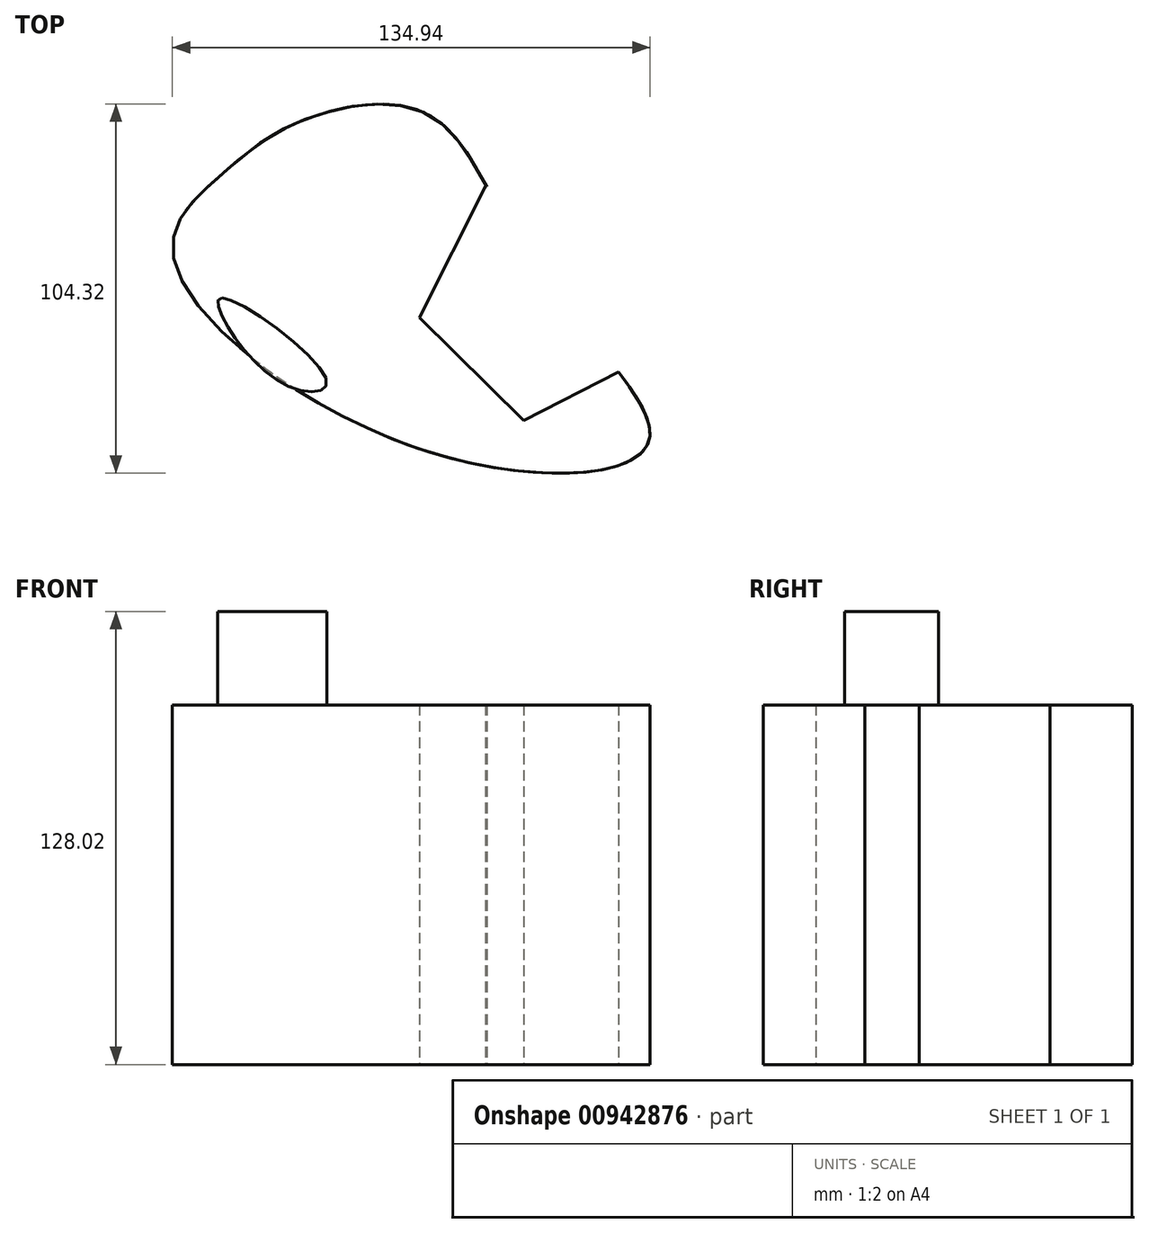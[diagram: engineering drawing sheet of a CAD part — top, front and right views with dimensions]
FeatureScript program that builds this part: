
annotation { "Feature Type Name" : "Feature", "Feature Type Description" : "" }
export const myFeature = defineFeature(function(context is Context, id is Id, definition is map)
    precondition{}
    {
        {
            var Q0;
            Q0=qCreatedBy(makeId("Top.planeOp"),FACE);
            var sketch = newSketch(context, id + "F0", { "sketchPlane" : qUnion([Q0])});
            skFitSpline(sketch, "E0", {"points": [v(-61.43, 8.67) * mm, v(11, -47.33) * mm, v(73.1, -44.16) * mm, v(40.48, 5.2) * mm, v(10.16, 48.33) * mm, v(-26.78, 45.54) * mm, v(-47.46, 31.25) * mm, v(-61.43, 8.67) * mm]});
            skFitSpline(sketch, "E1.0", {"points": [v(-54.93, 10.07) * mm, v(-54.88, 9.47) * mm, v(-54.78, 8.83) * mm, v(-54.57, 7.89) * mm, v(-54.17, 6.58) * mm, v(-53.41, 4.81) * mm, v(-52.05, 2.25) * mm, v(-49.67, -1.28) * mm, v(-45.82, -5.82) * mm, v(-41.07, -10.53) * mm, v(-35.53, -15.27) * mm, v(-29.3, -19.97) * mm, v(-20.25, -26.02) * mm, v(-10.25, -31.61) * mm, v(0.25, -36.41) * mm, v(6.93, -39.02) * mm, v(12.3, -40.83) * mm, v(17.67, -42.46) * mm, v(24.37, -44.13) * mm, v(32.22, -45.58) * mm, v(39.73, -46.47) * mm, v(46.72, -46.82) * mm, v(53.01, -46.64) * mm, v(58.42, -45.97) * mm, v(61.98, -45.07) * mm, v(64.13, -44.23) * mm, v(65.36, -43.59) * mm, v(66.19, -43) * mm, v(66.55, -42.64) * mm, v(66.7, -42.45) * mm, v(66.75, -42.36) * mm, v(66.76, -42.33) * mm, v(66.77, -42.31) * mm, v(66.77, -42.3) * mm, v(66.78, -42.26) * mm, v(66.8, -42.1) * mm, v(66.79, -41.64) * mm, v(66.58, -40.68) * mm, v(66.11, -39.36) * mm, v(65.36, -37.76) * mm, v(64, -35.32) * mm, v(61.64, -31.81) * mm, v(58.01, -27.09) * mm, v(53.8, -21.98) * mm, v(49.22, -16.56) * mm, v(45.27, -11.85) * mm, v(42.13, -7.98) * mm, v(39.8, -5.03) * mm, v(37.54, -2.05) * mm, v(35.71, 0.48) * mm, v(34.31, 2.51) * mm, v(32.96, 4.54) * mm, v(31.35, 7.06) * mm, v(29.54, 10.04) * mm, v(27.26, 13.95) * mm, v(24.65, 18.67) * mm, v(21.79, 23.98) * mm, v(19.1, 28.82) * mm, v(16.5, 33.1) * mm, v(13.93, 36.69) * mm, v(11.82, 39.05) * mm, v(10.12, 40.55) * mm, v(8.85, 41.5) * mm, v(7.77, 42.15) * mm, v(6.88, 42.6) * mm, v(5.94, 43) * mm, v(4.67, 43.44) * mm, v(2.45, 44) * mm, v(-0.66, 44.4) * mm, v(-4.78, 44.4) * mm, v(-9.11, 43.93) * mm, v(-13.51, 43.07) * mm, v(-17.1, 42.09) * mm, v(-19.84, 41.18) * mm, v(-21.82, 40.45) * mm, v(-23.7, 39.7) * mm, v(-25.44, 38.9) * mm, v(-27.08, 38.1) * mm, v(-29.14, 37) * mm, v(-31.53, 35.55) * mm, v(-34.22, 33.67) * mm, v(-36.86, 31.61) * mm, v(-39.11, 29.73) * mm, v(-41, 28.11) * mm, v(-42.46, 26.85) * mm, v(-43.99, 25.53) * mm, v(-45.5, 24.22) * mm, v(-46.97, 22.9) * mm, v(-48.85, 21.15) * mm, v(-50.97, 18.96) * mm, v(-52.64, 16.81) * mm, v(-53.64, 15.17) * mm, v(-54.21, 13.99) * mm, v(-54.62, 12.86) * mm, v(-54.86, 11.75) * mm, v(-54.94, 10.83) * mm, v(-54.93, 10.07) * mm, v(-54.88, 9.47) * mm, v(-54.78, 8.83) * mm, v(-54.93, 10.07) * mm]});
            skCircle(sketch, "E2.cCircle", {"center": v(43.03, -3.61) * mm, "radius": 28.54 * mm, "construction": true});
            skLineSegment(sketch, "E2.0", {"start": v(74.54, -19.48) * mm, "end": v(37.67, -38.48) * mm});
            skLineSegment(sketch, "E2.1", {"start": v(37.67, -38.48) * mm, "end": v(8.21, -9.3) * mm});
            skLineSegment(sketch, "E2.2", {"start": v(8.21, -9.3) * mm, "end": v(26.87, 27.75) * mm});
            skLineSegment(sketch, "E2.3", {"start": v(26.87, 27.75) * mm, "end": v(67.86, 21.45) * mm});
            skLineSegment(sketch, "E2.4", {"start": v(67.86, 21.45) * mm, "end": v(74.54, -19.48) * mm});
            skPoint(sketch, "E2.0.midPoint", {"position": v(56.1, -28.98) * mm});
            skSolve(sketch);
        }
        {
            var Q0;
            {var subQ5=sQuery(id+"F0.wireOp",EDGE,"E2.0");var subQ6=sQuery(id+"F0.wireOp",EDGE,"E0");var subQ7=makeQuery(id+"F0.imprint","INTERSECT",VERTEX,{"derivedFrom":[subQ6,subQ5]});Q0=makeQuery(id+"F0.imprint","IMPRINT",FACE,{"disambiguationData":[TD([[makeQuery(id+"F0.imprint","IMPRINT",EDGE,{"disambiguationData":[TD([[subQ7,1.0]])],"derivedFrom":subQ6}),1.0]])]});}
            extrude(context, id + "F1", {"entities" : qUnion([Q0]), "depth" : 25.4 * mm, "offsetDistance" : 25.4 * mm});
        }
        {
            var Q0;
            Q0=makeQuery(id+"F1.opExtrude","CAP_FACE",FACE,{"disambiguationData":[OSD([sQuery(id+"F0.wireOp",EDGE,"E0"),sQuery(id+"F0.wireOp",EDGE,"E1.0"),sQuery(id+"F0.wireOp",EDGE,"E2.0"),sQuery(id+"F0.wireOp",EDGE,"E2.2"),sQuery(id+"F0.wireOp",EDGE,"E2.3")])],"isStart":false});
            extrude(context, id + "F2", {"entities" : qUnion([Q0]), "operationType" : NewBodyOperationType.ADD, "depth" : 76.2 * mm, "offsetDistance" : 25.4 * mm});
        }
        {
            var Q0;
            Q0=makeQuery(id+"F2.opExtrude","CAP_FACE",FACE,{"disambiguationData":[OSD([sQuery(id+"F0.wireOp",EDGE,"E0"),sQuery(id+"F0.wireOp",EDGE,"E1.0"),sQuery(id+"F0.wireOp",EDGE,"E2.0"),sQuery(id+"F0.wireOp",EDGE,"E2.2"),sQuery(id+"F0.wireOp",EDGE,"E2.3")])],"isStart":false});
            var sketch = newSketch(context, id + "F3", { "sketchPlane" : qUnion([Q0])});
            skFitSpline(sketch, "E3", {"points": [v(-47.51, -3.79) * mm, v(-46.82, -10.35) * mm, v(-26.68, -29.6) * mm, v(-18, -27.16) * mm, v(-47.51, -3.79) * mm]});
            skSolve(sketch);
        }
        {
            var Q0;
            {var subQ0=sQuery(id+"F3.wireOp",EDGE,"E3");var subQ1=makeQuery(id+"F2.opExtrude","CAP_EDGE",EDGE,{"disambiguationData":[OSD([sQuery(id+"F0.wireOp",EDGE,"E0")])],"isStart":false});var subQ2=makeQuery(id+"F3.imprint","INTERSECT",VERTEX,{"disambiguationData":[OD(0.0)],"derivedFrom":[subQ1,subQ0]});Q0=makeQuery(id+"F3.imprint","IMPRINT",FACE,{"disambiguationData":[TD([[makeQuery(id+"F3.imprint","IMPRINT",EDGE,{"disambiguationData":[TD([[subQ2,-1.0]])],"derivedFrom":subQ0}),1.0]])]});}
            var Q1;
            {var subQ0=sQuery(id+"F3.wireOp",EDGE,"E3");var subQ1=makeQuery(id+"F2.opExtrude","CAP_EDGE",EDGE,{"disambiguationData":[OSD([sQuery(id+"F0.wireOp",EDGE,"E0")])],"isStart":false});var subQ2=makeQuery(id+"F3.imprint","INTERSECT",VERTEX,{"disambiguationData":[OD(0.0)],"derivedFrom":[subQ1,subQ0]});Q1=makeQuery(id+"F3.imprint","IMPRINT",FACE,{"disambiguationData":[TD([[makeQuery(id+"F3.imprint","IMPRINT",EDGE,{"disambiguationData":[TD([[subQ2,1.0]])],"derivedFrom":subQ0}),1.0]])]});}
            extrude(context, id + "F4", {"entities" : qUnion([Q0, Q1]), "operationType" : NewBodyOperationType.ADD, "depth" : 26.42 * mm, "offsetDistance" : 25.4 * mm});
        }
    });
